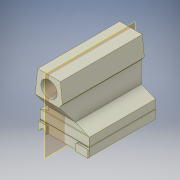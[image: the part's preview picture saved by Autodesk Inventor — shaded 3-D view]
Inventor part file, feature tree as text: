
AUTODESK INVENTOR PART (.ipt)
format: ipt  version: 2016 (Build 200138000, 138)  size: 308,736 bytes
history: native  units: mm
features: extrude x17, sketch x17, fillet x3, plane x1
ambient origin geometry x8: Origin, YZ Plane, XZ Plane, XY Plane, X Axis, Y Axis, Z Axis, Center Point
bodies: Solid1 (feature_tree)
feature tree (38):
  extrude  "Extrusion1"  Depth=151.0mm
  extrude  "Extrusion2"  Depth=25.0mm
  extrude  "Extrusion3"  Depth=22.68928mm
  extrude  "Extrusion4"  Depth=10.0mm
  extrude  "Extrusion5"  Depth=25.0mm
  extrude  "Extrusion6"  Depth=2.0mm TaperAngle=0.0deg
  fillet  "Fillet1"  Radius=37.0mm
  extrude  "Extrusion7"  Depth=1.0mm TaperAngle=0.0deg
  fillet  "Fillet3"  Radius=5.0mm
  extrude  "Extrusion8"  Depth=5.0mm
  extrude  "Extrusion9"  Depth=1.0mm
  extrude  "Extrusion10"  Depth=1.0mm
  extrude  "Extrusion11"  Depth=26.0mm TaperAngle=0.0deg
  plane  "Work Plane1"
  extrude  "Extrusion12"  Depth=152.0mm TaperAngle=0.0deg
  extrude  "Extrusion13"  Depth=35.0mm
  extrude  "Extrusion14"  Depth=16.755161mm
  extrude  "Extrusion15"  Depth=295.5mm TaperAngle=0.0deg
  fillet  "Fillet4"  Radius=295.5mm
  extrude  "Extrusion16"  Depth=295.5mm TaperAngle=0.0deg
  extrude  "Extrusion17"  Depth=2.0mm
  sketch  "Sketch1"  dims[d19=26.0mm d20=151.0mm]
  sketch  "Sketch2"  dims[d21=203.0mm d22=0.0mm d23=25.0mm]
  sketch  "Sketch3"  dims[d29=4.0mm d30=22.68928mm]
  sketch  "Sketch4"  dims[d31=8.726646mm d32=10.0mm]
  sketch  "Sketch5"  dims[d33=215.0mm d34=0.0mm d35=25.0mm]
  sketch  "Sketch6"  dims[d36=6.0mm d37=0.0mm d38=2.0mm d39=0.0mm d40=37.0mm]
  sketch  "Sketch8"  dims[d41=6.0mm d42=0.0mm d43=1.0mm d44=0.0mm d45=5.0mm]
  sketch  "Sketch9"  dims[d47=1.0mm d48=0.0mm d49=5.0mm]
  sketch  "Sketch10"  dims[d50=1.0mm d51=1.0mm]
  sketch  "Sketch11"  dims[d52=1.0mm d53=1.0mm]
  sketch  "Sketch12"  dims[d54=1.0mm d55=0.0mm d56=26.0mm d57=0.0mm]
  sketch  "Sketch13"  dims[d58=49.0mm d59=152.0mm d60=0.0mm]
  sketch  "Sketch14"  dims[d61=35.0mm d62=35.0mm]
  sketch  "Sketch15"  dims[d63=16.755161mm d64=16.755161mm]
  sketch  "Sketch16"  dims[d65=58.0mm d66=295.5mm d67=0.0mm d68=295.5mm d69=0.0mm]
  sketch  "Sketch18"  dims[d70=295.5mm d71=0.0mm d72=295.5mm d73=0.0mm]
  sketch  "Sketch19"  dims[d74=1.0mm d75=0.0mm d76=2.0mm d85=1.0mm d86=0.0mm d87=50.0mm d88=300.0mm d89=0.0mm]
